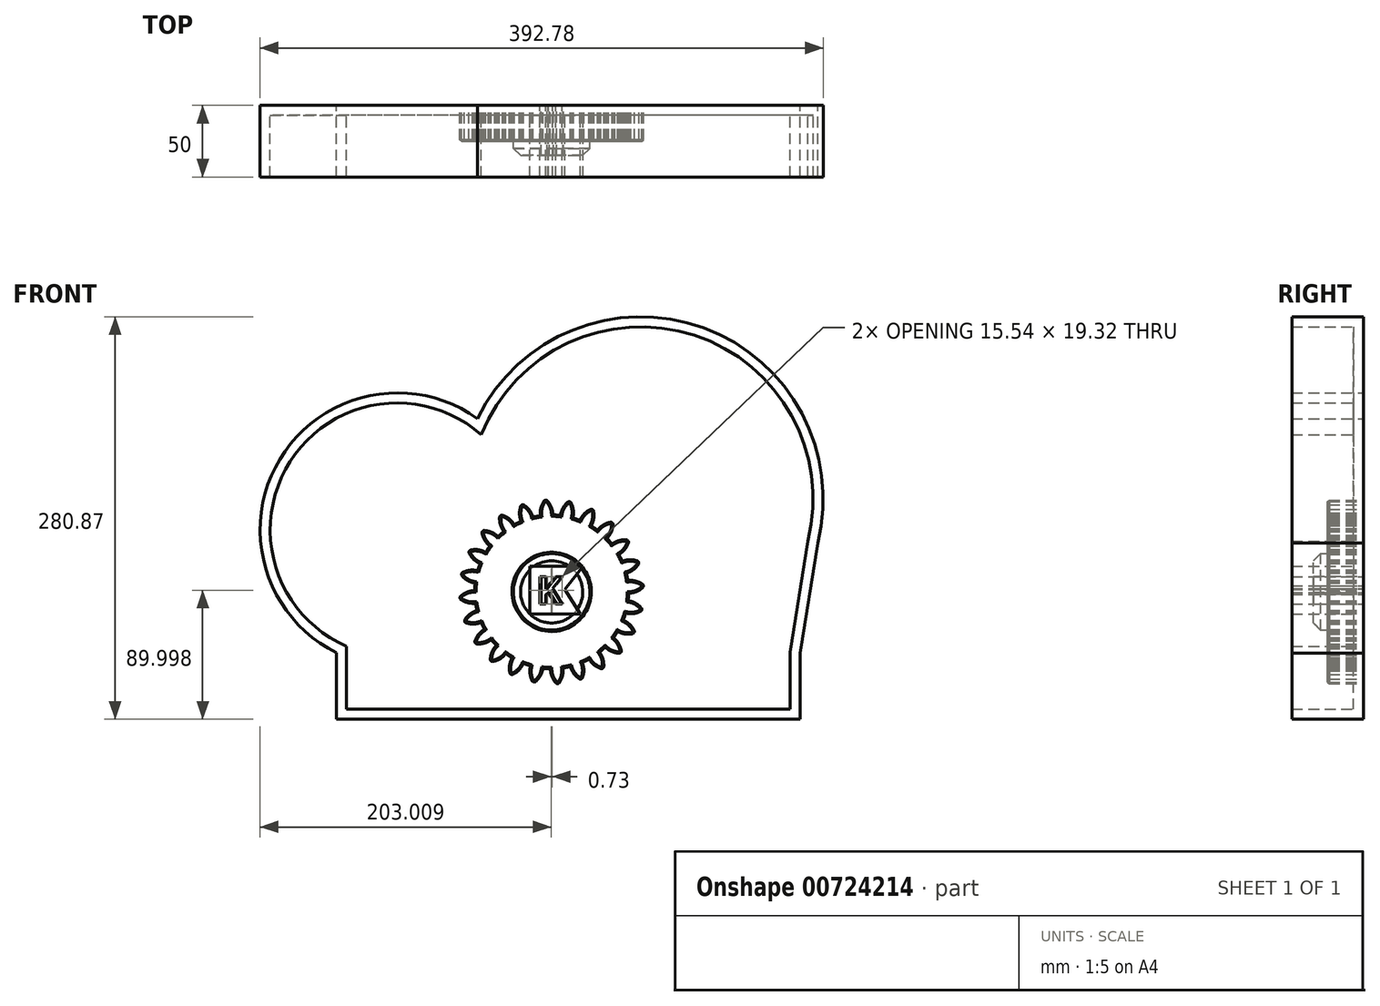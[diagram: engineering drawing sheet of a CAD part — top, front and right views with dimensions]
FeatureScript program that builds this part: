
annotation { "Feature Type Name" : "Feature", "Feature Type Description" : "" }
export const myFeature = defineFeature(function(context is Context, id is Id, definition is map)
    precondition{}
    {
        {
            var Q0;
            Q0=qCreatedBy(makeId("Front.planeOp"),FACE);
            var sketch = newSketch(context, id + "F0", { "sketchPlane" : qUnion([Q0])});
            skCircle(sketch, "E0", {"center": v(0, 0) * mm, "radius": 53.72 * mm});
            skCircle(sketch, "E1", {"center": v(0, 0) * mm, "radius": 58.67 * mm, "construction": true});
            skCircle(sketch, "E2", {"center": v(0, 0) * mm, "radius": 63.5 * mm, "construction": true});
            skLineSegment(sketch, "E3", {"start": v(0, 0) * mm, "end": v(0, 75.31) * mm, "construction": true});
            skLineSegment(sketch, "E4", {"start": v(0, 0) * mm, "end": v(-4.94, 75.31) * mm, "construction": true});
            skLineSegment(sketch, "E5", {"start": v(0, 58.67) * mm, "end": v(-66.03, 58.67) * mm, "construction": true});
            skLineSegment(sketch, "E6", {"start": v(0, 58.67) * mm, "end": v(-58.84, 37.26) * mm, "construction": true});
            skCircle(sketch, "E7", {"center": v(0, 0) * mm, "radius": 55.14 * mm, "construction": true});
            skCircle(sketch, "E8", {"center": v(0, 58.67) * mm, "radius": 14.6 * mm, "construction": true});
            skCircle(sketch, "E9", {"center": v(-13.72, 53.68) * mm, "radius": 14.6 * mm, "construction": true});
            skArc(sketch, "E10", {"start": v(0, 58.67) * mm, "mid": v(-1.2, 61.19) * mm, "end": v(-2.86, 63.44) * mm});
            skArc(sketch, "E11", {"start": v(0.8, 55.13) * mm, "mid": v(0.52, 56.93) * mm, "end": v(0, 58.67) * mm});
            skArc(sketch, "E12", {"start": v(0.88, 53.71) * mm, "mid": v(0.86, 54.42) * mm, "end": v(0.8, 55.13) * mm});
            skArc(sketch, "E13.MirrorCS", {"start": v(-7.66, 58.17) * mm, "mid": v(-6.79, 60.82) * mm, "end": v(-5.45, 63.27) * mm});
            skArc(sketch, "E14.MirrorCS", {"start": v(-8, 54.55) * mm, "mid": v(-7.95, 56.37) * mm, "end": v(-7.66, 58.17) * mm});
            skArc(sketch, "E15", {"start": v(-2.86, 63.44) * mm, "mid": v(-4.2, 63.98) * mm, "end": v(-5.45, 63.27) * mm});
            skArc(sketch, "E16.MirrorCS", {"start": v(-7.88, 53.14) * mm, "mid": v(-7.96, 53.84) * mm, "end": v(-8, 54.55) * mm});
            skCircle(sketch, "E17", {"center": v(0, 0) * mm, "radius": 26.67 * mm});
            skText(sketch, "E18", { "text": "K", "fontName": "OpenSans-Bold.ttf"});
            const initialGuessF0  = {"E18": [-0.00984, -0.00845, 1, 0, 0.01948]};
            skSetInitialGuess(sketch, initialGuessF0);
            skSolve(sketch);
        }
        {
            var Q0;
            {var subQ0=sQuery(id+"F0.wireOp",EDGE,"E0");var subQ1=makeQuery(id+"F0.imprint","INTERSECT",VERTEX,{"derivedFrom":[subQ0,sQuery(id+"F0.wireOp",EDGE,"E12")]});Q0=makeQuery(id+"F0.imprint","IMPRINT",FACE,{"disambiguationData":[TD([[makeQuery(id+"F0.imprint","IMPRINT",EDGE,{"disambiguationData":[TD([[subQ1,-1.0]])],"derivedFrom":subQ0}),1.0]])]});}
            var Q1;
            Q1=makeQuery(id+"F0.imprint","IMPRINT",FACE,{"disambiguationData":[TD([[makeQuery(id+"F0.imprint","IMPRINT",EDGE,{"derivedFrom":sQuery(id+"F0.wireOp",EDGE,"E10")}),1.0]])]});
            extrude(context, id + "F1", {"entities" : qUnion([Q0, Q1]), "depth" : 25 * mm, "offsetDistance" : 25 * mm});
        }
        {
            var Q0;
            Q0=makeQuery(id+"F1.opExtrude","CAP_EDGE",EDGE,{"disambiguationData":[OSD([sQuery(id+"F0.wireOp",EDGE,"E0")])],"isStart":false});
            var Q1;
            Q1=makeQuery(id+"F1.opExtrude","CAP_EDGE",EDGE,{"disambiguationData":[OSD([sQuery(id+"F0.wireOp",EDGE,"E10")])],"isStart":false});
            var Q2;
            Q2=makeQuery(id+"F1.opExtrude","CAP_EDGE",EDGE,{"disambiguationData":[OSD([sQuery(id+"F0.wireOp",EDGE,"E14.MirrorCS")])],"isStart":false});
            var Q3;
            Q3=makeQuery(id+"F1.opExtrude","CAP_FACE",FACE,{"disambiguationData":[OSD([sQuery(id+"F0.wireOp",EDGE,"E0"),sQuery(id+"F0.wireOp",EDGE,"E10"),sQuery(id+"F0.wireOp",EDGE,"E11"),sQuery(id+"F0.wireOp",EDGE,"E12"),sQuery(id+"F0.wireOp",EDGE,"E13.MirrorCS"),sQuery(id+"F0.wireOp",EDGE,"E14.MirrorCS"),sQuery(id+"F0.wireOp",EDGE,"E15"),sQuery(id+"F0.wireOp",EDGE,"E16.MirrorCS"),sQuery(id+"F0.wireOp",EDGE,"E17")])],"isStart":false});
            chamfer(context, id + "F2", {"entities" : qUnion([Q0, Q1, Q2, Q3]), "width" : 1 * mm, "tangentPropagation" : true});
        }
        {
            var Q0;
            Q0=makeQuery(id+"F1.opExtrude","SWEPT_BODY",BODY,{"disambiguationData":[OSD([sQuery(id+"F0.wireOp",EDGE,"E0"),sQuery(id+"F0.wireOp",EDGE,"E10"),sQuery(id+"F0.wireOp",EDGE,"E11"),sQuery(id+"F0.wireOp",EDGE,"E12"),sQuery(id+"F0.wireOp",EDGE,"E13.MirrorCS"),sQuery(id+"F0.wireOp",EDGE,"E14.MirrorCS"),sQuery(id+"F0.wireOp",EDGE,"E15"),sQuery(id+"F0.wireOp",EDGE,"E16.MirrorCS"),sQuery(id+"F0.wireOp",EDGE,"E17")])]});
            var Q1;
            Q1=makeQuery(id+"F1.opExtrude","SWEPT_FACE",FACE,{"disambiguationData":[OSD([sQuery(id+"F0.wireOp",EDGE,"E0")])]});
            circularPattern(context, id + "F3", {"entities" : qUnion([Q0]), "axis" : qUnion([Q1]), "angle" : 360 * degree, "instanceCount" : 24, "equalSpace" : true});
        }
        {
            var Q0;
            Q0=makeQuery(id+"F0.imprint","IMPRINT",FACE,{"disambiguationData":[TD([[makeQuery(id+"F0.imprint","IMPRINT",EDGE,{"derivedFrom":sQuery(id+"F0.wireOp",EDGE,"E17")}),1.0]])]});
            extrude(context, id + "F4", {"entities" : qUnion([Q0]), "operationType" : NewBodyOperationType.ADD, "depth" : 35 * mm, "offsetDistance" : 25 * mm});
        }
        {
            var Q0;
            Q0=makeQuery(id+"F4.opExtrude","CAP_EDGE",EDGE,{"disambiguationData":[OSD([sQuery(id+"F0.wireOp",EDGE,"E17")])],"isStart":false});
            chamfer(context, id + "F5", {"entities" : qUnion([Q0]), "width" : 5 * mm, "tangentPropagation" : true});
        }
        {
            var Q0;
            Q0=qCreatedBy(makeId("Front.planeOp"),FACE);
            var sketch = newSketch(context, id + "F6", { "sketchPlane" : qUnion([Q0])});
            skLineSegment(sketch, "E19", {"start": v(173.45, -88.9) * mm, "end": v(-150.13, -88.9) * mm});
            skLineSegment(sketch, "E20", {"start": v(-150.13, -88.9) * mm, "end": v(-150.13, -42.48) * mm});
            skLineSegment(sketch, "E21", {"start": v(173.45, -88.9) * mm, "end": v(173.45, -42.6) * mm});
            skArc(sketch, "E22", {"start": v(-51.86, 120.86) * mm, "mid": v(-189.7, 92.56) * mm, "end": v(-150.13, -42.48) * mm});
            skArc(sketch, "E23", {"start": v(185.63, 34.1) * mm, "mid": v(105.89, 184.25) * mm, "end": v(-51.86, 120.86) * mm});
            skLineSegment(sketch, "E24", {"start": v(185.63, 34.1) * mm, "end": v(173.45, -42.6) * mm});
            skText(sketch, "E25", { "text": "K", "fontName": "OpenSans-Bold.ttf"});
            const initialGuessF6  = {"E25": [-0.01057, -0.00857, 1, 0, 0.01948]};
            skSetInitialGuess(sketch, initialGuessF6);
            skSolve(sketch);
        }
        {
            var Q0;
            Q0=makeQuery(id+"F6.imprint","IMPRINT",FACE,{"disambiguationData":[TD([[makeQuery(id+"F6.imprint","IMPRINT",EDGE,{"derivedFrom":sQuery(id+"F6.wireOp",EDGE,"E19")}),-1.0]])]});
            extrude(context, id + "F7", {"entities" : qUnion([Q0]), "depth" : 50 * mm, "offsetDistance" : 25 * mm});
        }
        {
            var Q0;
            Q0=makeQuery(id+"F7.opExtrude","CAP_FACE",FACE,{"disambiguationData":[OSD([sQuery(id+"F6.wireOp",EDGE,"E19"),sQuery(id+"F6.wireOp",EDGE,"E20"),sQuery(id+"F6.wireOp",EDGE,"E21"),sQuery(id+"F6.wireOp",EDGE,"E22"),sQuery(id+"F6.wireOp",EDGE,"E23"),sQuery(id+"F6.wireOp",EDGE,"E24")])],"isStart":false});
            shell(context, id + "F8", {"entities" : qUnion([Q0]), "thickness" : 7 * mm});
        }
    });
